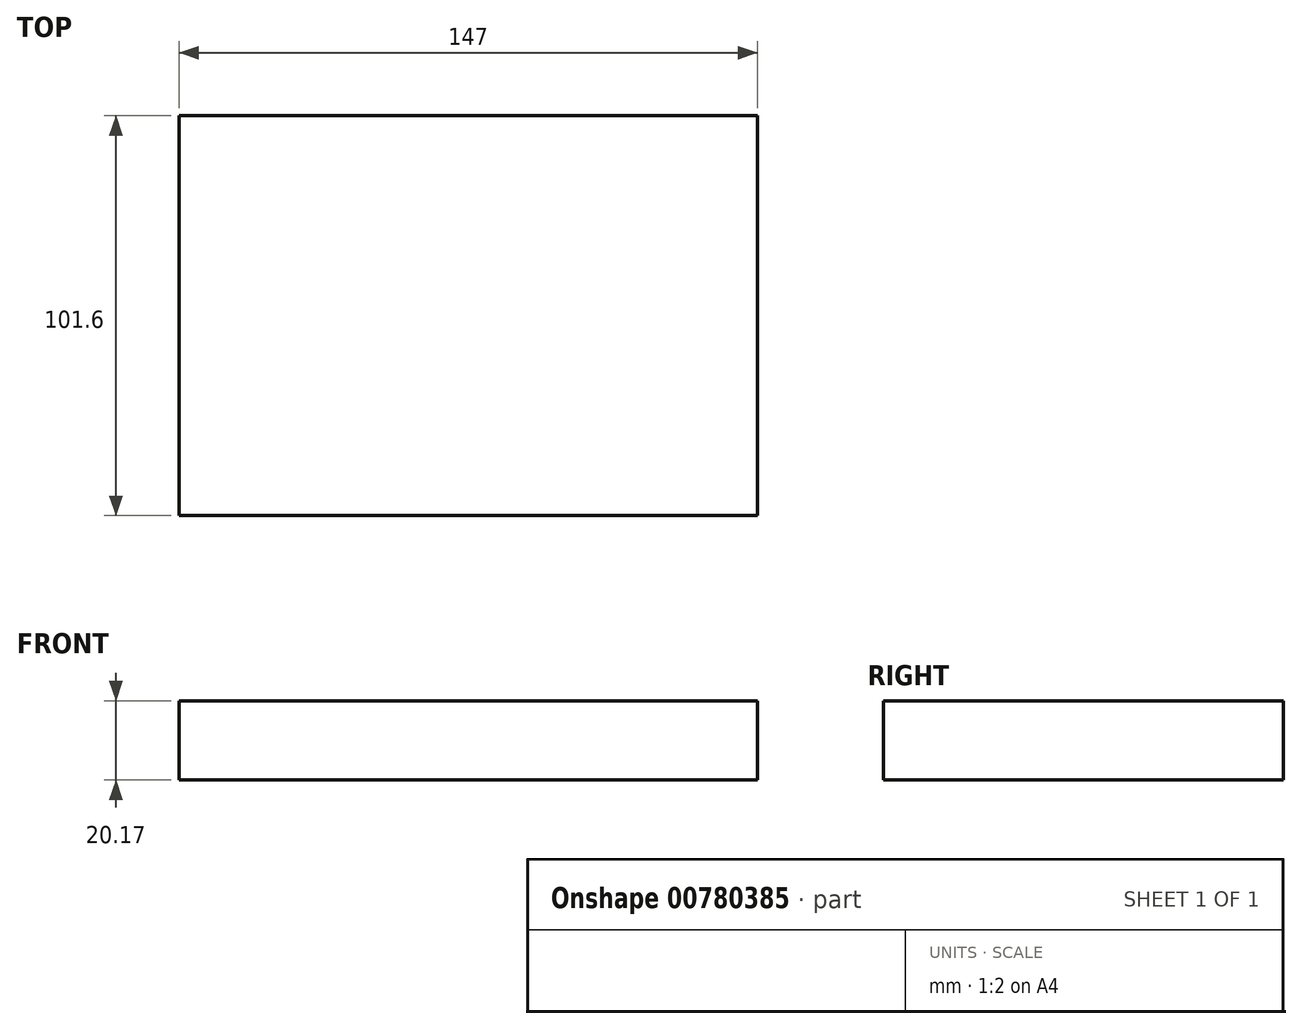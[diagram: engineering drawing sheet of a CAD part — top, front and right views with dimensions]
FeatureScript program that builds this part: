
annotation { "Feature Type Name" : "Feature", "Feature Type Description" : "" }
export const myFeature = defineFeature(function(context is Context, id is Id, definition is map)
    precondition{}
    {
        {
            var Q0;
            Q0=qCreatedBy(makeId("Top.planeOp"),FACE);
            var sketch = newSketch(context, id + "F0", { "sketchPlane" : qUnion([Q0])});
            skLineSegment(sketch, "E0.bottom", {"start": v(73.5, -50.8) * mm, "end": v(-73.5, -50.8) * mm});
            skLineSegment(sketch, "E0.top", {"start": v(73.5, 50.8) * mm, "end": v(-73.5, 50.8) * mm});
            skLineSegment(sketch, "E0.left", {"start": v(73.5, -50.8) * mm, "end": v(73.5, 50.8) * mm});
            skLineSegment(sketch, "E0.right", {"start": v(-73.5, -50.8) * mm, "end": v(-73.5, 50.8) * mm});
            skPoint(sketch, "E0.middle", {"position": v(0, 0) * mm});
            skSolve(sketch);
        }
        {
            var Q0;
            Q0=makeQuery(id+"F0.imprint","IMPRINT",FACE,{"disambiguationData":[TD([[makeQuery(id+"F0.imprint","IMPRINT",EDGE,{"derivedFrom":sQuery(id+"F0.wireOp",EDGE,"E0.bottom")}),-1.0]])]});
            extrude(context, id + "F1", {"entities" : qUnion([Q0]), "depth" : 20.17 * mm, "offsetDistance" : 25 * mm});
        }
    });
